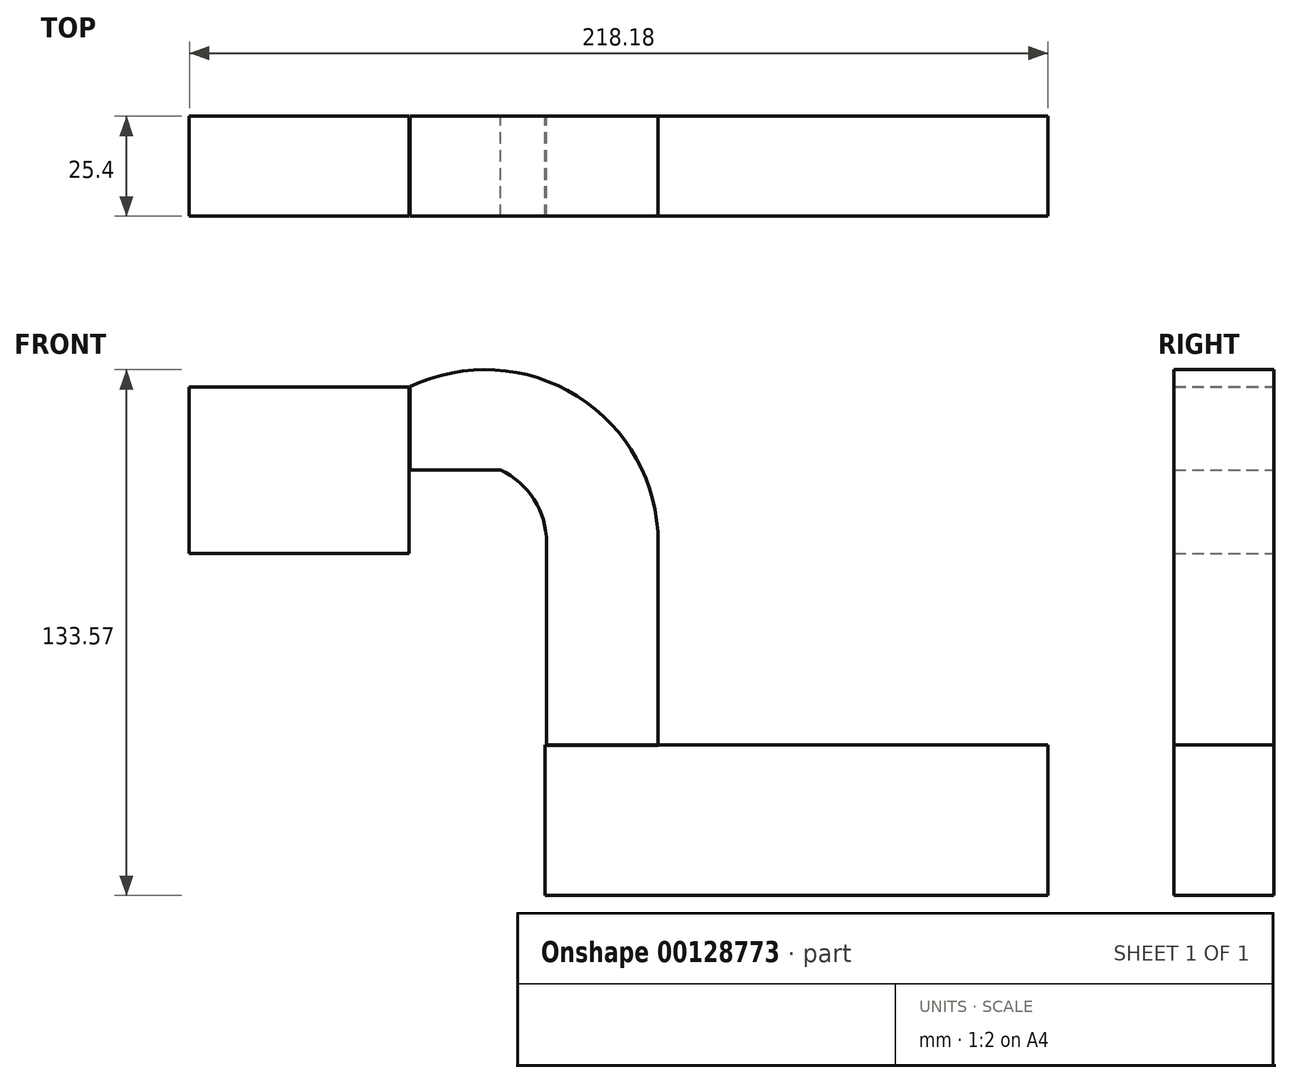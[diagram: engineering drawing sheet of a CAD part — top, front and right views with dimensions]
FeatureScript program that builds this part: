
annotation { "Feature Type Name" : "Feature", "Feature Type Description" : "" }
export const myFeature = defineFeature(function(context is Context, id is Id, definition is map)
    precondition{}
    {
        {
            var Q0;
            Q0=qCreatedBy(makeId("Front.planeOp"),FACE);
            var sketch = newSketch(context, id + "F0", { "sketchPlane" : qUnion([Q0])});
            skLineSegment(sketch, "E0.bottom", {"start": v(-63.88, 19.12) * mm, "end": v(63.88, 19.12) * mm});
            skLineSegment(sketch, "E0.top", {"start": v(-63.88, -19.12) * mm, "end": v(63.88, -19.12) * mm});
            skLineSegment(sketch, "E0.left", {"start": v(-63.88, 19.12) * mm, "end": v(-63.88, -19.12) * mm});
            skLineSegment(sketch, "E0.right", {"start": v(63.88, 19.12) * mm, "end": v(63.88, -19.12) * mm});
            skPoint(sketch, "E0.middle", {"position": v(0, 0) * mm});
            skLineSegment(sketch, "E1.bottom", {"start": v(-154.3, 67.7) * mm, "end": v(-98.52, 67.7) * mm});
            skLineSegment(sketch, "E1.top", {"start": v(-154.3, 110) * mm, "end": v(-98.52, 110) * mm});
            skLineSegment(sketch, "E1.left", {"start": v(-154.3, 67.7) * mm, "end": v(-154.3, 110) * mm});
            skLineSegment(sketch, "E1.right", {"start": v(-98.52, 67.7) * mm, "end": v(-98.52, 110) * mm});
            skPoint(sketch, "E1.middle", {"position": v(-126.41, 88.85) * mm});
            skLineSegment(sketch, "E2", {"start": v(-63.88, 19.12) * mm, "end": v(-63.88, 61.4) * mm});
            skArc(sketch, "E3", {"start": v(-63.88, 61.4) * mm, "mid": v(-78.57, 79.01) * mm, "end": v(-98.52, 67.7) * mm});
            skSolve(sketch);
        }
        {
            var Q0;
            Q0=qCreatedBy(makeId("Front.planeOp"),FACE);
            var sketch = newSketch(context, id + "F1", { "sketchPlane" : qUnion([Q0])});
            skLineSegment(sketch, "E4.bottom", {"start": v(-63.54, -19) * mm, "end": v(63.54, -19) * mm});
            skLineSegment(sketch, "E4.top", {"start": v(-63.54, 19) * mm, "end": v(63.54, 19) * mm});
            skLineSegment(sketch, "E4.left", {"start": v(-63.54, -19) * mm, "end": v(-63.54, 19) * mm});
            skLineSegment(sketch, "E4.right", {"start": v(63.54, -19) * mm, "end": v(63.54, 19) * mm});
            skPoint(sketch, "E4.middle", {"position": v(0, 0) * mm});
            skLineSegment(sketch, "E5.bottom", {"start": v(-153.97, 67.82) * mm, "end": v(-98.18, 67.82) * mm});
            skLineSegment(sketch, "E5.top", {"start": v(-153.97, 110.1) * mm, "end": v(-98.18, 110.1) * mm});
            skLineSegment(sketch, "E5.left", {"start": v(-153.97, 67.82) * mm, "end": v(-153.97, 110.1) * mm});
            skLineSegment(sketch, "E5.right", {"start": v(-98.18, 67.82) * mm, "end": v(-98.18, 110.1) * mm});
            skPoint(sketch, "E5.middle", {"position": v(-126.08, 88.96) * mm});
            skLineSegment(sketch, "E6", {"start": v(-63.54, 19) * mm, "end": v(-63.54, 70.52) * mm});
            skArc(sketch, "E7", {"start": v(-63.54, 70.52) * mm, "mid": v(-66.71, 81.44) * mm, "end": v(-75.24, 88.96) * mm});
            skLineSegment(sketch, "E8", {"start": v(-75.24, 88.96) * mm, "end": v(-126.08, 88.96) * mm});
            skLineSegment(sketch, "E9", {"start": v(-35.2, 19) * mm, "end": v(-35.2, 70.52) * mm});
            skArc(sketch, "E10", {"start": v(-35.2, 70.52) * mm, "mid": v(-55.76, 107.71) * mm, "end": v(-98.18, 110.1) * mm});
            skSolve(sketch);
        }
        {
            var Q0;
            Q0 = qSketchRegion(id + "F0", true);
            var Q1;
            {var subQ0=sQuery(id+"F1.wireOp",EDGE,"E6");Q1=makeQuery(id+"F1.imprint","IMPRINT",FACE,{"disambiguationData":[TD([[makeQuery(id+"F1.imprint","IMPRINT",EDGE,{"derivedFrom":subQ0}),-1.0]])]});}
            extrude(context, id + "F2", {"entities" : qUnion([Q0, Q1]), "depth" : 25.4 * mm});
        }
        {
            var Q0;
            Q0 = qSketchRegion(id + "F0", true);
            extrude(context, id + "F3", {"entities" : qUnion([Q0]), "depth" : 25.4 * mm});
        }
    });
